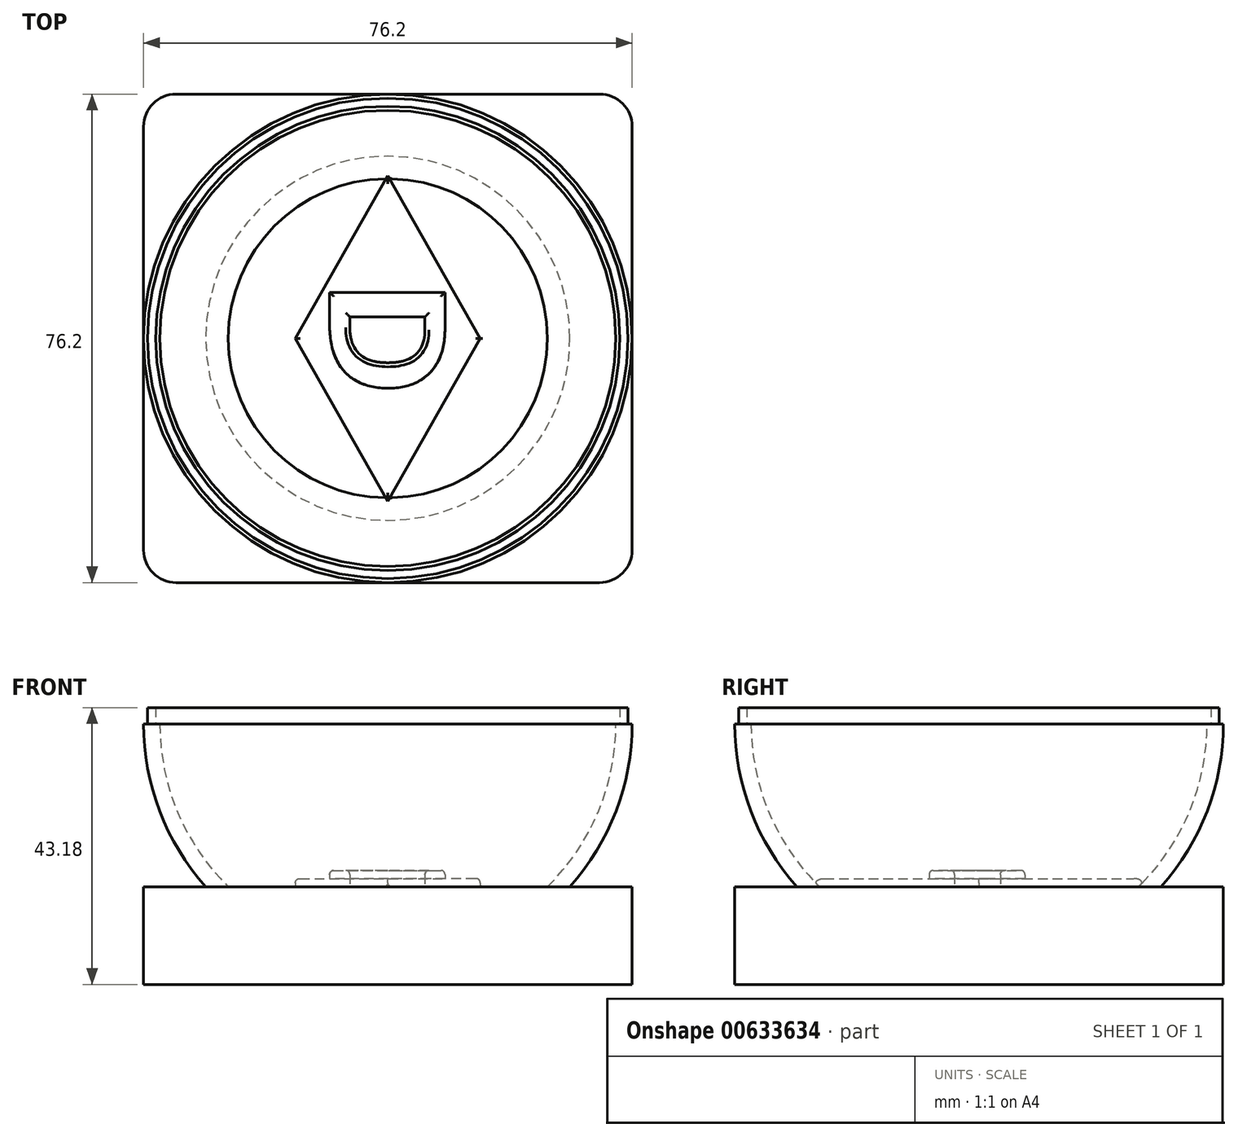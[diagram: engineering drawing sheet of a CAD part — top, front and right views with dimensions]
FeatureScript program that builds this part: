
annotation { "Feature Type Name" : "Feature", "Feature Type Description" : "" }
export const myFeature = defineFeature(function(context is Context, id is Id, definition is map)
    precondition{}
    {
        {
            var Q0;
            Q0=qCreatedBy(makeId("Top.planeOp"),FACE);
            var sketch = newSketch(context, id + "F0", { "sketchPlane" : qUnion([Q0])});
            skArc(sketch, "E0", {"start": v(0, -38.1) * mm, "mid": v(38.1, 0) * mm, "end": v(0, 38.1) * mm});
            skLineSegment(sketch, "E1", {"start": v(0, -38.1) * mm, "end": v(0, 38.1) * mm});
            skSolve(sketch);
        }
        {
            var Q0;
            Q0 = qSketchRegion(id + "F0", true);
            var Q1;
            Q1=sQuery(id+"F0.wireOp",EDGE,"E1");
            revolve(context, id + "F1", {"entities" : qUnion([Q0]), "axis" : qUnion([Q1]), "revolveType" : RevolveType.ONE_DIRECTION, "angle" : 180 * degree});
        }
        {
            var Q0;
            Q0=qCreatedBy(makeId("Top.planeOp"),FACE);
            cPlane(context, id + "F2", {"entities" : qUnion([Q0]), "cplaneType" : CPlaneType.OFFSET, "offset" : 25.4 * mm, "oppositeDirection" : true, "width" : 152.4 * mm, "height" : 152.4 * mm});
        }
        {
            var Q0;
            Q0=qCreatedBy(id+"F2.planeOp",FACE);
            var sketch = newSketch(context, id + "F3", { "sketchPlane" : qUnion([Q0])});
            skLineSegment(sketch, "E2.bottom", {"start": v(38.1, 38.1) * mm, "end": v(-38.1, 38.1) * mm});
            skLineSegment(sketch, "E2.top", {"start": v(38.1, -38.1) * mm, "end": v(-38.1, -38.1) * mm});
            skLineSegment(sketch, "E2.left", {"start": v(38.1, 38.1) * mm, "end": v(38.1, -38.1) * mm});
            skLineSegment(sketch, "E2.right", {"start": v(-38.1, 38.1) * mm, "end": v(-38.1, -38.1) * mm});
            skPoint(sketch, "E2.middle", {"position": v(0, 0) * mm});
            skCircle(sketch, "E3", {"center": v(0, 0) * mm, "radius": 38.1 * mm});
            skSolve(sketch);
        }
        {
            var Q0;
            Q0=makeQuery(id+"F1.opRevolve","CAP_FACE",FACE,{"disambiguationData":[OSD([sQuery(id+"F0.wireOp",EDGE,"E0"),sQuery(id+"F0.wireOp",EDGE,"E1")])],"isStart":true});
            shell(context, id + "F4", {"entities" : qUnion([Q0]), "thickness" : 2.54 * mm});
        }
        {
            var Q0;
            Q0=qCreatedBy(makeId("Right.planeOp"),FACE);
            var sketch = newSketch(context, id + "F5", { "sketchPlane" : qUnion([Q0])});
            skLineSegment(sketch, "E4.bottom", {"start": v(38.1, -25.4) * mm, "end": v(-38.1, -25.4) * mm});
            skLineSegment(sketch, "E4.top", {"start": v(38.1, -40.64) * mm, "end": v(-38.1, -40.64) * mm});
            skLineSegment(sketch, "E4.left", {"start": v(38.1, -25.4) * mm, "end": v(38.1, -40.64) * mm});
            skLineSegment(sketch, "E4.right", {"start": v(-38.1, -25.4) * mm, "end": v(-38.1, -40.64) * mm});
            skPoint(sketch, "E4.middle", {"position": v(0, -33.02) * mm});
            skSolve(sketch);
        }
        {
            var Q0;
            Q0 = qSketchRegion(id + "F5", true);
            extrude(context, id + "F6", {"entities" : qUnion([Q0]), "operationType" : NewBodyOperationType.ADD, "depth" : 38.1 * mm, "offsetDistance" : 25.4 * mm, "hasSecondDirection" : true, "secondDirectionOppositeDirection" : true, "secondDirectionDepth" : 38.1 * mm});
        }
        {
            var Q0;
            {var subQ0=sQuery(id+"F3.wireOp",EDGE,"E3");var subQ1=makeQuery(id+"F3.imprint","INTERSECT",VERTEX,{"derivedFrom":[sQuery(id+"F3.wireOp",EDGE,"E2.bottom"),subQ0]});Q0=makeQuery(id+"F3.imprint","IMPRINT",FACE,{"disambiguationData":[TD([[makeQuery(id+"F3.imprint","IMPRINT",EDGE,{"disambiguationData":[TD([[subQ1,1.0]])],"derivedFrom":subQ0}),1.0]])]});}
            var sketch = newSketch(context, id + "F7", { "sketchPlane" : qUnion([Q0])});
            skLineSegment(sketch, "E5.0", {"start": v(-14.42, 0) * mm, "end": v(0, 25.4) * mm});
            skLineSegment(sketch, "E5.1", {"start": v(0, 25.4) * mm, "end": v(14.42, 0) * mm});
            skLineSegment(sketch, "E5.2", {"start": v(14.42, 0) * mm, "end": v(0, -25.4) * mm});
            skLineSegment(sketch, "E5.3", {"start": v(0, -25.4) * mm, "end": v(-14.42, 0) * mm});
            skPoint(sketch, "E5.0.midPoint", {"position": v(-7.21, 12.7) * mm});
            skText(sketch, "E6", { "text": "D", "fontName": "OpenSans-Bold.ttf"});
            const initialGuessF7  = {"E6": [-0.00908, 0.00942, 0, -1, 0.01815]};
            skSetInitialGuess(sketch, initialGuessF7);
            skSolve(sketch);
        }
        {
            var Q0;
            Q0=makeQuery(id+"F7.imprint","IMPRINT",FACE,{"disambiguationData":[TD([[makeQuery(id+"F7.imprint","IMPRINT",EDGE,{"derivedFrom":sQuery(id+"F7.wireOp",EDGE,"E6.sketch_text.stroke-0")}),-1.0]])]});
            extrude(context, id + "F8", {"entities" : qUnion([Q0]), "operationType" : NewBodyOperationType.ADD, "depth" : 2.54 * mm, "offsetDistance" : 25.4 * mm});
        }
        {
            var Q0;
            Q0 = qSketchRegion(id + "F7", true);
            extrude(context, id + "F9", {"entities" : qUnion([Q0]), "operationType" : NewBodyOperationType.ADD, "depth" : 1.27 * mm, "offsetDistance" : 25.4 * mm});
        }
        {
            var Q0;
            Q0=makeQuery(id+"F9.opExtrude","CAP_EDGE",EDGE,{"disambiguationData":[OSD([sQuery(id+"F7.wireOp",EDGE,"E5.1")])],"isStart":false});
            var Q1;
            Q1=makeQuery(id+"F9.opExtrude","CAP_EDGE",EDGE,{"disambiguationData":[OSD([sQuery(id+"F7.wireOp",EDGE,"E5.2")])],"isStart":false});
            var Q2;
            Q2=makeQuery(id+"F9.opExtrude","CAP_EDGE",EDGE,{"disambiguationData":[OSD([sQuery(id+"F7.wireOp",EDGE,"E5.0")])],"isStart":false});
            var Q3;
            Q3=makeQuery(id+"F9.opExtrude","CAP_EDGE",EDGE,{"disambiguationData":[OSD([sQuery(id+"F7.wireOp",EDGE,"E5.3")])],"isStart":false});
            fillet(context, id + "F10", {"entities" : qUnion([Q0, Q1, Q2, Q3]), "radius" : 0.64 * mm, "tangentPropagation" : true, "allowEdgeOverflow" : false});
        }
        {
            var Q0;
            Q0=makeQuery(id+"F8.opExtrude","CAP_FACE",FACE,{"disambiguationData":[OSD([sQuery(id+"F7.wireOp",EDGE,"E6.sketch_text.stroke-0"),sQuery(id+"F7.wireOp",EDGE,"E6.sketch_text.stroke-1"),sQuery(id+"F7.wireOp",EDGE,"E6.sketch_text.stroke-2"),sQuery(id+"F7.wireOp",EDGE,"E6.sketch_text.stroke-3"),sQuery(id+"F7.wireOp",EDGE,"E6.sketch_text.stroke-4"),sQuery(id+"F7.wireOp",EDGE,"E6.sketch_text.stroke-5"),sQuery(id+"F7.wireOp",EDGE,"E6.sketch_text.stroke-6"),sQuery(id+"F7.wireOp",EDGE,"E6.sketch_text.stroke-7"),sQuery(id+"F7.wireOp",EDGE,"E6.sketch_text.stroke-8"),sQuery(id+"F7.wireOp",EDGE,"E6.sketch_text.stroke-9"),sQuery(id+"F7.wireOp",EDGE,"E6.sketch_text.stroke-10"),sQuery(id+"F7.wireOp",EDGE,"E6.sketch_text.stroke-11")])],"isStart":false});
            fillet(context, id + "F11", {"entities" : qUnion([Q0]), "radius" : 0.64 * mm, "tangentPropagation" : true, "allowEdgeOverflow" : false});
        }
        {
            var Q0;
            Q0=makeQuery(id+"F6.opExtrude","CAP_EDGE",EDGE,{"disambiguationData":[OSD([sQuery(id+"F5.wireOp",EDGE,"E4.left")])],"isStart":true});
            var Q1;
            Q1=makeQuery(id+"F6.opExtrude","CAP_EDGE",EDGE,{"disambiguationData":[OSD([sQuery(id+"F5.wireOp",EDGE,"E4.right")])],"isStart":true});
            var Q2;
            Q2=makeQuery(id+"F6.opExtrude","CAP_EDGE",EDGE,{"disambiguationData":[OSD([sQuery(id+"F5.wireOp",EDGE,"E4.left")])],"isStart":false});
            var Q3;
            Q3=makeQuery(id+"F6.opExtrude","CAP_EDGE",EDGE,{"disambiguationData":[OSD([sQuery(id+"F5.wireOp",EDGE,"E4.right")])],"isStart":false});
            fillet(context, id + "F12", {"entities" : qUnion([Q0, Q1, Q2, Q3]), "radius" : 5.08 * mm, "tangentPropagation" : true, "allowEdgeOverflow" : false});
        }
        {
            var Q0;
            Q0=makeQuery(id+"F1.opRevolve","CAP_FACE",FACE,{"disambiguationData":[OSD([sQuery(id+"F0.wireOp",EDGE,"E0"),sQuery(id+"F0.wireOp",EDGE,"E1")])],"isStart":true});
            var sketch = newSketch(context, id + "F13", { "sketchPlane" : qUnion([Q0])});
            skCircle(sketch, "E7.0", {"center": v(0, 0) * mm, "radius": 36.2 * mm});
            skCircle(sketch, "E8.0", {"center": v(0, 0) * mm, "radius": 37.47 * mm});
            skSolve(sketch);
        }
        {
            var Q0;
            Q0 = qSketchRegion(id + "F13", true);
            extrude(context, id + "F14", {"entities" : qUnion([Q0]), "operationType" : NewBodyOperationType.ADD, "depth" : 2.54 * mm, "offsetDistance" : 25.4 * mm});
        }
        {
            var Q0;
            Q0=makeQuery(id+"F9.opExtrude","CAP_EDGE",EDGE,{"disambiguationData":[OSD([sQuery(id+"F7.wireOp",EDGE,"E5.1")])],"isStart":true});
            var Q1;
            Q1=makeQuery(id+"F9.opExtrude","CAP_EDGE",EDGE,{"disambiguationData":[OSD([sQuery(id+"F7.wireOp",EDGE,"E5.2")])],"isStart":true});
            var Q2;
            Q2=makeQuery(id+"F9.opExtrude","CAP_EDGE",EDGE,{"disambiguationData":[OSD([sQuery(id+"F7.wireOp",EDGE,"E5.3")])],"isStart":true});
            var Q3;
            Q3=makeQuery(id+"F9.opExtrude","CAP_EDGE",EDGE,{"disambiguationData":[OSD([sQuery(id+"F7.wireOp",EDGE,"E5.0")])],"isStart":true});
            fillet(context, id + "F15", {"entities" : qUnion([Q0, Q1, Q2, Q3]), "radius" : 0.32 * mm, "tangentPropagation" : true, "allowEdgeOverflow" : false});
        }
    });
